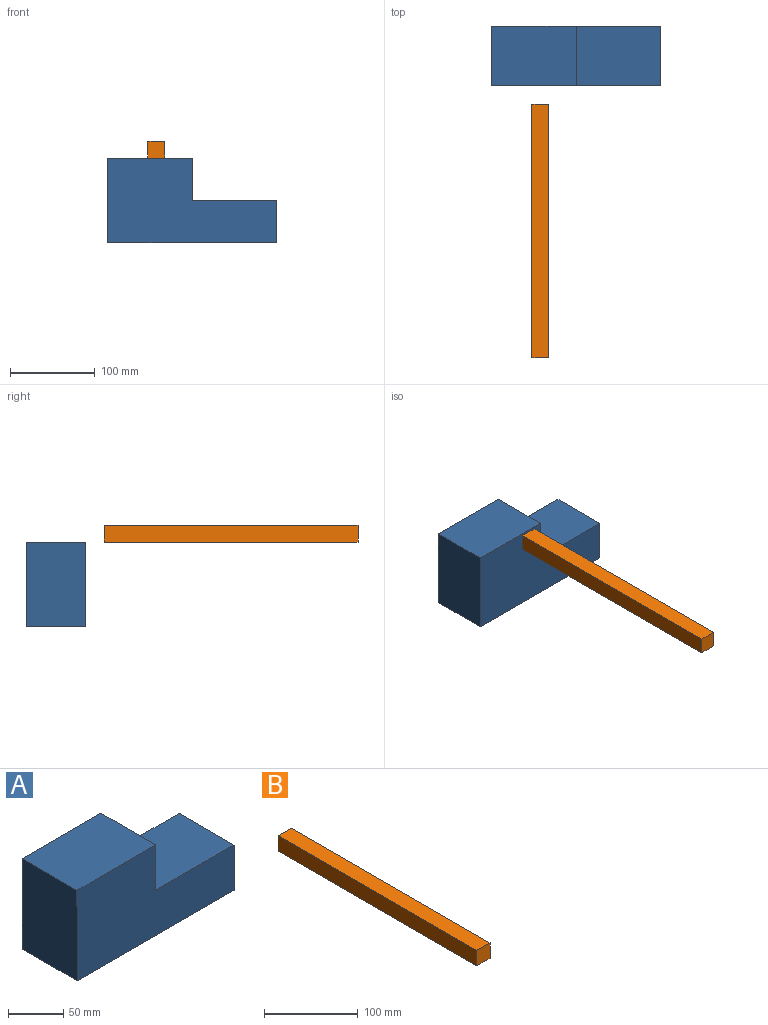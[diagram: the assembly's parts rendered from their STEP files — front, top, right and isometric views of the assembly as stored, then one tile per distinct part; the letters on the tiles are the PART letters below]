
ASSEMBLY  parts=2 mates=1
PART A: 8 faces, bbox 200.2x70x100 mm
  f0: plane 199.68x70mm, normal (0,0,-1), area 13977.6mm2, adj f1,f5,f6,f7
  f1: plane 70x50mm, normal (1,0,0), area 3500mm2, adj f0,f2,f6,f7
  f2: plane 99.68x70mm, normal (0,0,1), area 6977.7mm2, adj f1,f3,f6,f7
  f3: plane 70x50mm, normal (1,0,0), area 3499.9mm2, adj f2,f4,f6,f7
  f4: plane 100.48x70mm, normal (0,0,1), area 7033.3mm2, adj f3,f5,f6,f7
  f5: plane 100x70mm, normal (-1,0,0), area 7000mm2, adj f0,f4,f6,f7
  f6: plane 200.16x100mm, normal (0,1,0), area 15007.7mm2, adj f0,f1,f2,f3,f4,f5
  f7: plane 200.16x100mm, normal (0,-1,0), area 15007.7mm2, adj f0,f1,f2,f3,f4,f5
PART B: 6 faces, bbox 19.9x300x20 mm
  f0: plane 300x19.87mm, normal (0,0,-1), area 5961.9mm2, adj f1,f3,f4,f5
  f1: plane 300x20mm, normal (1,0,0), area 5999.9mm2, adj f0,f2,f4,f5
  f2: plane 300x19.75mm, normal (0,0,1), area 5923.9mm2, adj f1,f3,f4,f5
  f3: plane 300x20mm, normal (-1,0,0.01), area 6000mm2, adj f0,f2,f4,f5
  f4: plane 20x19.87mm, normal (0,-1,0), area 396.2mm2, adj f0,f1,f2,f3
  f5: plane 20x19.87mm, normal (0,1,0), area 396.2mm2, adj f0,f1,f2,f3
PLACE A at identity fixed
PLACE B rot(axis=(0,1,0),90deg) t=(-52.64,-22.7,99.84)mm
MATE planar B.f1 <-> A.f4  axis (0,0,-1) through (-42.64,-172.7,99.84)mm
